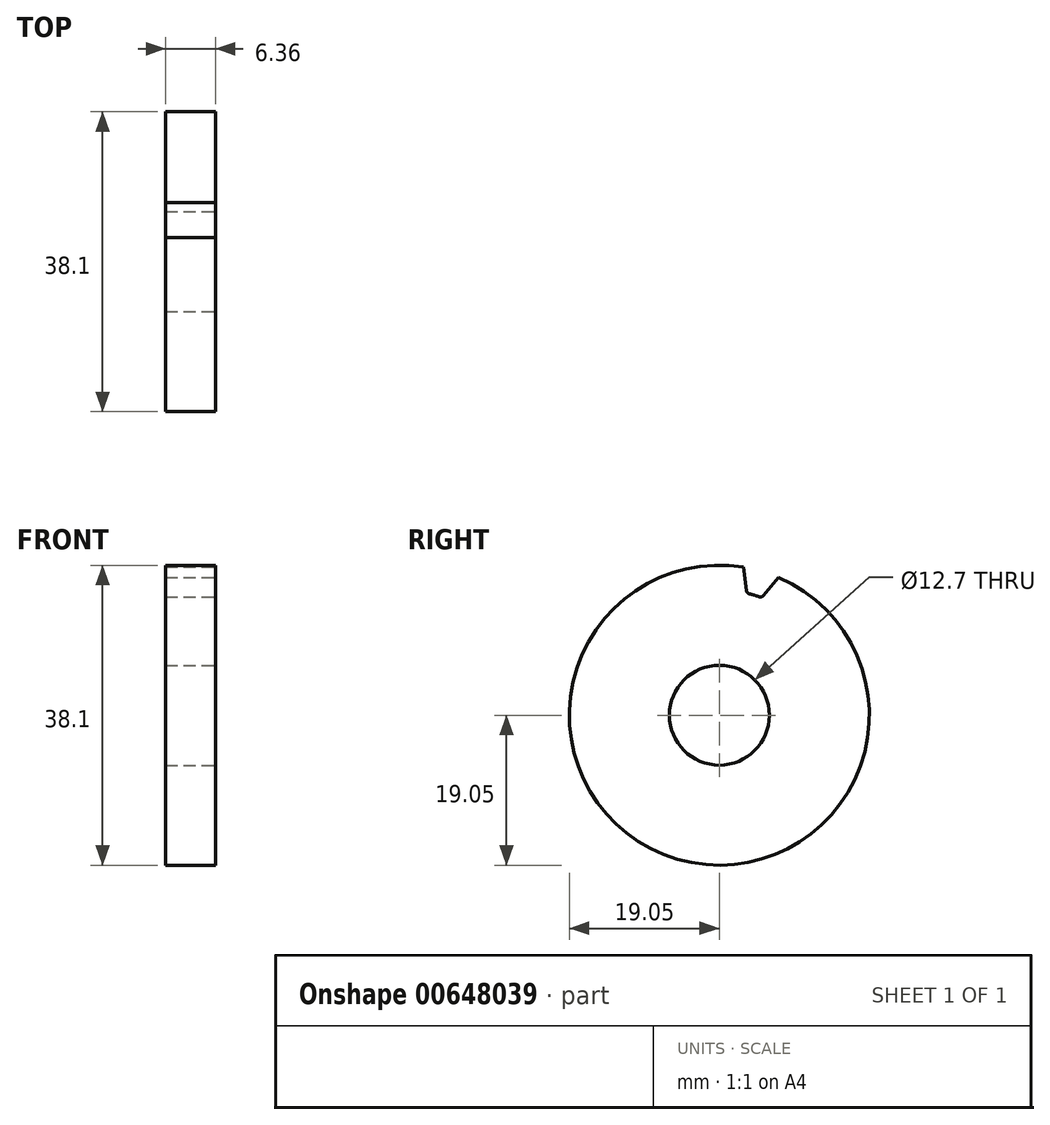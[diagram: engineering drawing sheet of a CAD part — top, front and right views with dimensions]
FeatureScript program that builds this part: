
annotation { "Feature Type Name" : "Feature", "Feature Type Description" : "" }
export const myFeature = defineFeature(function(context is Context, id is Id, definition is map)
    precondition{}
    {
        {
            var Q0;
            Q0=qCreatedBy(makeId("Right.planeOp"),FACE);
            var sketch = newSketch(context, id + "F0", { "sketchPlane" : qUnion([Q0])});
            skCircle(sketch, "E0", {"center": v(0, 0) * mm, "radius": 19.05 * mm});
            skSolve(sketch);
        }
        {
            var Q0;
            Q0=makeQuery(id+"F0.imprint","IMPRINT",FACE,{"disambiguationData":[TD([[makeQuery(id+"F0.imprint","IMPRINT",EDGE,{"derivedFrom":sQuery(id+"F0.wireOp",EDGE,"E0")}),1.0]])]});
            extrude(context, id + "F1", {"entities" : qUnion([Q0]), "endBound" : BoundingType.SYMMETRIC, "depth" : 6.35 * mm, "offsetDistance" : 25.4 * mm});
        }
        {
            var Q0;
            Q0=makeQuery(id+"F1.opExtrude","CAP_FACE",FACE,{"disambiguationData":[OSD([sQuery(id+"F0.wireOp",EDGE,"E0")])],"isStart":false});
            var sketch = newSketch(context, id + "F2", { "sketchPlane" : qUnion([Q0])});
            skLineSegment(sketch, "E1", {"start": v(0, 21.9) * mm, "end": v(0, 0) * mm, "construction": true});
            skLineSegment(sketch, "E2", {"start": v(3.05, 18.8) * mm, "end": v(3.48, 15.49) * mm});
            skCircle(sketch, "E3", {"center": v(0, 0) * mm, "radius": 15.88 * mm, "construction": true});
            skArc(sketch, "E4", {"start": v(5.4, 14.93) * mm, "mid": v(4.44, 15.24) * mm, "end": v(3.48, 15.49) * mm});
            skLineSegment(sketch, "E5", {"start": v(3.48, 15.49) * mm, "end": v(0, 0) * mm, "construction": true});
            skLineSegment(sketch, "E6", {"start": v(5.4, 14.93) * mm, "end": v(0, 0) * mm, "construction": true});
            skLineSegment(sketch, "E7", {"start": v(5.4, 14.93) * mm, "end": v(7.53, 17.5) * mm});
            skLineSegment(sketch, "E8", {"start": v(5.4, 14.93) * mm, "end": v(8.2, 22.71) * mm, "construction": true});
            skLineSegment(sketch, "E9", {"start": v(3.48, 15.49) * mm, "end": v(5.07, 22.6) * mm, "construction": true});
            skArc(sketch, "E10", {"start": v(7.53, 17.5) * mm, "mid": v(5.75, 19.73) * mm, "end": v(3.05, 18.8) * mm});
            skSolve(sketch);
        }
        {
            var Q0;
            Q0 = qSketchRegion(id + "F2", true);
            extrude(context, id + "F3", {"entities" : qUnion([Q0]), "operationType" : NewBodyOperationType.REMOVE, "endBound" : BoundingType.UP_TO_NEXT, "oppositeDirection" : true, "depth" : 25.4 * mm, "offsetDistance" : 25.4 * mm});
        }
        {
            var Q0;
            Q0=makeQuery(id+"F3.boolean.opBoolean","COPY",EDGE,{"derivedFrom":makeQuery(id+"F3.opExtrude","SWEPT_EDGE",EDGE,{"disambiguationData":[OSD([sQuery(id+"F2.wireOp",EDGE,"E2"),sQuery(id+"F2.wireOp",EDGE,"E4")])]})});
            var Q1;
            Q1=makeQuery(id+"F3.boolean.opBoolean","COPY",EDGE,{"derivedFrom":makeQuery(id+"F3.opExtrude","SWEPT_EDGE",EDGE,{"disambiguationData":[OSD([sQuery(id+"F2.wireOp",EDGE,"E4"),sQuery(id+"F2.wireOp",EDGE,"E7")])]})});
            var Q2;
            Q2=makeQuery(id+"F3.boolean.opBoolean","COPY",EDGE,{"derivedFrom":makeQuery(id+"F3.opExtrude","TWEAK_EDGE",EDGE,{"derivedFrom":[makeQuery(id+"F1.opExtrude","SWEPT_FACE",FACE,{"disambiguationData":[OSD([sQuery(id+"F0.wireOp",EDGE,"E0")])]}),makeQuery(id+"F2.imprint","IMPRINT",EDGE,{"derivedFrom":sQuery(id+"F2.wireOp",EDGE,"E2")})]})});
            var Q3;
            Q3=makeQuery(id+"F3.boolean.opBoolean","COPY",EDGE,{"derivedFrom":makeQuery(id+"F3.opExtrude","TWEAK_EDGE",EDGE,{"derivedFrom":[makeQuery(id+"F1.opExtrude","SWEPT_FACE",FACE,{"disambiguationData":[OSD([sQuery(id+"F0.wireOp",EDGE,"E0")])]}),makeQuery(id+"F2.imprint","IMPRINT",EDGE,{"derivedFrom":sQuery(id+"F2.wireOp",EDGE,"E7")})]})});
            fillet(context, id + "F4", {"entities" : qUnion([Q0, Q1, Q2, Q3]), "radius" : 0.5 * mm, "tangentPropagation" : true, "allowEdgeOverflow" : false});
        }
        {
            var Q0;
            Q0=makeQuery(id+"F1.opExtrude","CAP_FACE",FACE,{"disambiguationData":[OSD([sQuery(id+"F0.wireOp",EDGE,"E0")])],"isStart":false});
            var sketch = newSketch(context, id + "F5", { "sketchPlane" : qUnion([Q0])});
            skCircle(sketch, "E11", {"center": v(0, 0) * mm, "radius": 6.35 * mm});
            skSolve(sketch);
        }
        {
            var Q0;
            Q0 = qSketchRegion(id + "F5", true);
            extrude(context, id + "F6", {"entities" : qUnion([Q0]), "operationType" : NewBodyOperationType.REMOVE, "endBound" : BoundingType.UP_TO_NEXT, "oppositeDirection" : true, "depth" : 25.4 * mm, "offsetDistance" : 25.4 * mm});
        }
    });
